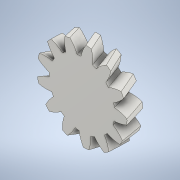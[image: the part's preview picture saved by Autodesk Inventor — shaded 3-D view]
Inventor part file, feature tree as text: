
AUTODESK INVENTOR PART (.ipt)
format: ipt  version: 2020 (Build 240168000, 168)  size: 342,016 bytes
history: native  units: mm (DEFAULTED — no unit token found)
features: plane x3, other x3, sketch x2, extrude x1
ambient origin geometry x8: Origin, YZ Plane, XZ Plane, XY Plane, X Axis, Y Axis, Z Axis, Center Point
bodies: Solid1 (feature_tree)
feature tree (9):
  extrude  "Extrusion1"  Depth=5.0mm TaperAngle=0.0deg
  plane  "Work Plane2"
  plane  "Work Plane8"
  plane  "Work Plane9"
  other  "Spur Gear"
  sketch  "Sketch1"  dims[d0=28.421824mm d1=5.0mm d2=0.0mm]
  sketch  "Sketch2"  dims[d3=25.0mm d4=10.0mm d5=0.0mm d16=25.0mm d17=0.0mm d34=2.41661mm d39=0.0mm d41=0.0mm d43=25.0mm d46=25.0mm d47=0.0mm d48=0.0mm]
  other  "Srf1"
  other  "Pitch Diameter"
